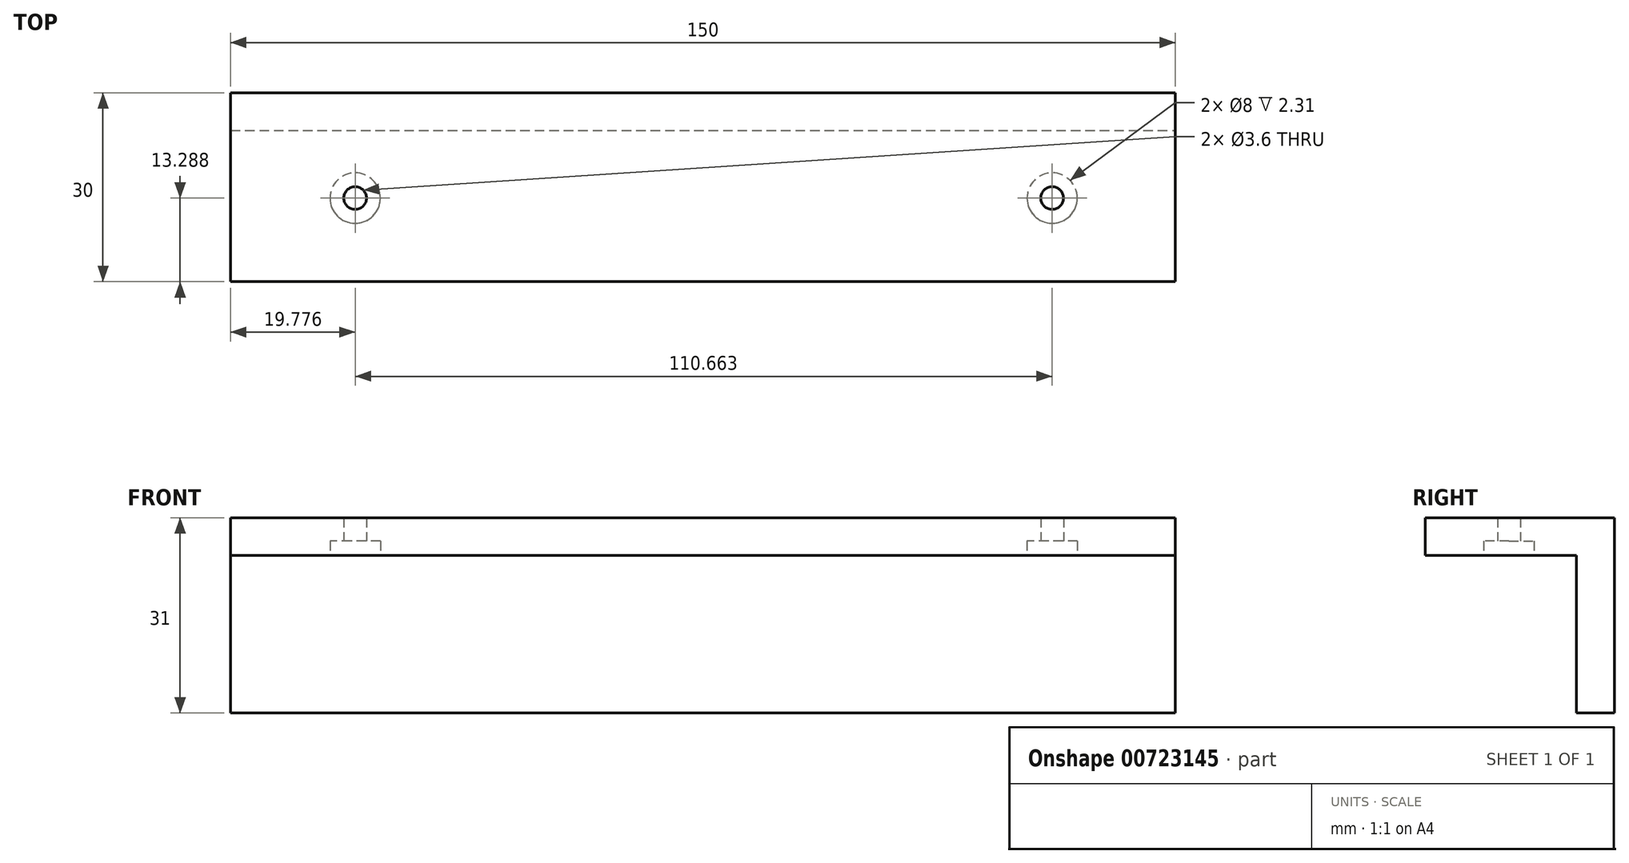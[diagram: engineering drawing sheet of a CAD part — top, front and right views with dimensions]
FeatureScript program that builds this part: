
annotation { "Feature Type Name" : "Feature", "Feature Type Description" : "" }
export const myFeature = defineFeature(function(context is Context, id is Id, definition is map)
    precondition{}
    {
        {
            var Q0;
            Q0=qCreatedBy(makeId("Front.planeOp"),FACE);
            var sketch = newSketch(context, id + "F0", { "sketchPlane" : qUnion([Q0])});
            skLineSegment(sketch, "E0", {"start": v(-38.58, 25) * mm, "end": v(-38.58, 0) * mm});
            skLineSegment(sketch, "E1", {"start": v(-38.58, 0) * mm, "end": v(111.42, 0) * mm});
            skLineSegment(sketch, "E2", {"start": v(111.42, 0) * mm, "end": v(111.42, 25) * mm});
            skLineSegment(sketch, "E3", {"start": v(111.42, 25) * mm, "end": v(-38.58, 25) * mm});
            skLineSegment(sketch, "E4", {"start": v(111.42, 25) * mm, "end": v(111.42, 31) * mm});
            skLineSegment(sketch, "E5", {"start": v(111.42, 31) * mm, "end": v(-38.58, 31) * mm});
            skLineSegment(sketch, "E6", {"start": v(-38.58, 31) * mm, "end": v(-38.58, 25) * mm});
            skSolve(sketch);
        }
        {
            var Q0;
            Q0=qSketchRegion(id+"F0",true);
            extrude(context, id + "F1", {"entities" : qUnion([Q0]), "depth" : 6 * mm, "offsetDistance" : 25 * mm});
        }
        {
            var Q0;
            Q0=makeQuery(id+"F0.imprint","IMPRINT",FACE,{"disambiguationData":[TD([[makeQuery(id+"F0.imprint","IMPRINT",EDGE,{"derivedFrom":sQuery(id+"F0.wireOp",EDGE,"E3")}),-1.0]])]});
            extrude(context, id + "F2", {"entities" : qUnion([Q0]), "operationType" : NewBodyOperationType.ADD, "depth" : 30 * mm, "offsetDistance" : 25 * mm});
        }
        {
            var Q0;
            Q0=qCreatedBy(makeId("Top.planeOp"),FACE);
            var sketch = newSketch(context, id + "F3", { "sketchPlane" : qUnion([Q0])});
            skLineSegment(sketch, "E7", {"start": v(-22.06, -0.64) * mm, "end": v(127.48, -0.64) * mm});
            skCircle(sketch, "E8", {"center": v(-18.8, -16.71) * mm, "radius": 1.8 * mm});
            skCircle(sketch, "E9", {"center": v(91.86, -16.71) * mm, "radius": 1.8 * mm});
            skLineSegment(sketch, "E10", {"start": v(-18.8, -16.71) * mm, "end": v(-38.47, -16.71) * mm, "construction": true});
            skLineSegment(sketch, "E11", {"start": v(91.86, -16.71) * mm, "end": v(111.53, -16.71) * mm, "construction": true});
            skLineSegment(sketch, "E12", {"start": v(-38.47, -16.71) * mm, "end": v(-38.47, -30.2) * mm, "construction": true});
            skLineSegment(sketch, "E13", {"start": v(-38.47, -30.2) * mm, "end": v(111.53, -30.2) * mm, "construction": true});
            skLineSegment(sketch, "E14", {"start": v(111.53, -30.2) * mm, "end": v(111.53, -16.71) * mm, "construction": true});
            skLineSegment(sketch, "E15", {"start": v(-18.8, -16.71) * mm, "end": v(91.86, -16.71) * mm, "construction": true});
            skCircle(sketch, "E16", {"center": v(-18.8, -16.71) * mm, "radius": 4 * mm});
            skCircle(sketch, "E17", {"center": v(91.86, -16.71) * mm, "radius": 4 * mm});
            skSolve(sketch);
        }
        {
            var Q0;
            Q0=makeQuery(id+"F3.imprint","IMPRINT",FACE,{"disambiguationData":[TD([[makeQuery(id+"F3.imprint","IMPRINT",EDGE,{"derivedFrom":sQuery(id+"F3.wireOp",EDGE,"E9")}),-1.0]])]});
            var Q1;
            Q1=makeQuery(id+"F3.imprint","IMPRINT",FACE,{"disambiguationData":[TD([[makeQuery(id+"F3.imprint","IMPRINT",EDGE,{"derivedFrom":sQuery(id+"F3.wireOp",EDGE,"E8")}),-1.0]])]});
            extrude(context, id + "F4", {"entities" : qUnion([Q0, Q1]), "operationType" : NewBodyOperationType.REMOVE, "oppositeDirection" : true, "depth" : -27.3 * mm, "offsetDistance" : 25 * mm});
        }
        {
            var Q0;
            Q0=makeQuery(id+"F4.boolean.opBoolean","SPLIT",FACE,{"disambiguationData":[TD([makeQuery(id+"F4.opExtrude","SWEPT_FACE",FACE,{"disambiguationData":[OSD([sQuery(id+"F3.wireOp",EDGE,"E8")])]})])],"derivedFrom":makeQuery(id+"F2.opExtrude","SWEPT_FACE",FACE,{"disambiguationData":[OSD([sQuery(id+"F0.wireOp",EDGE,"E3")])]})});
            var Q1;
            Q1=makeQuery(id+"F4.boolean.opBoolean","SPLIT",FACE,{"disambiguationData":[TD([makeQuery(id+"F4.opExtrude","SWEPT_FACE",FACE,{"disambiguationData":[OSD([sQuery(id+"F3.wireOp",EDGE,"E9")])]})])],"derivedFrom":makeQuery(id+"F2.opExtrude","SWEPT_FACE",FACE,{"disambiguationData":[OSD([sQuery(id+"F0.wireOp",EDGE,"E3")])]})});
            extrude(context, id + "F5", {"entities" : qUnion([Q0, Q1]), "operationType" : NewBodyOperationType.REMOVE, "oppositeDirection" : true, "depth" : 25 * mm, "offsetDistance" : 25 * mm});
        }
    });
